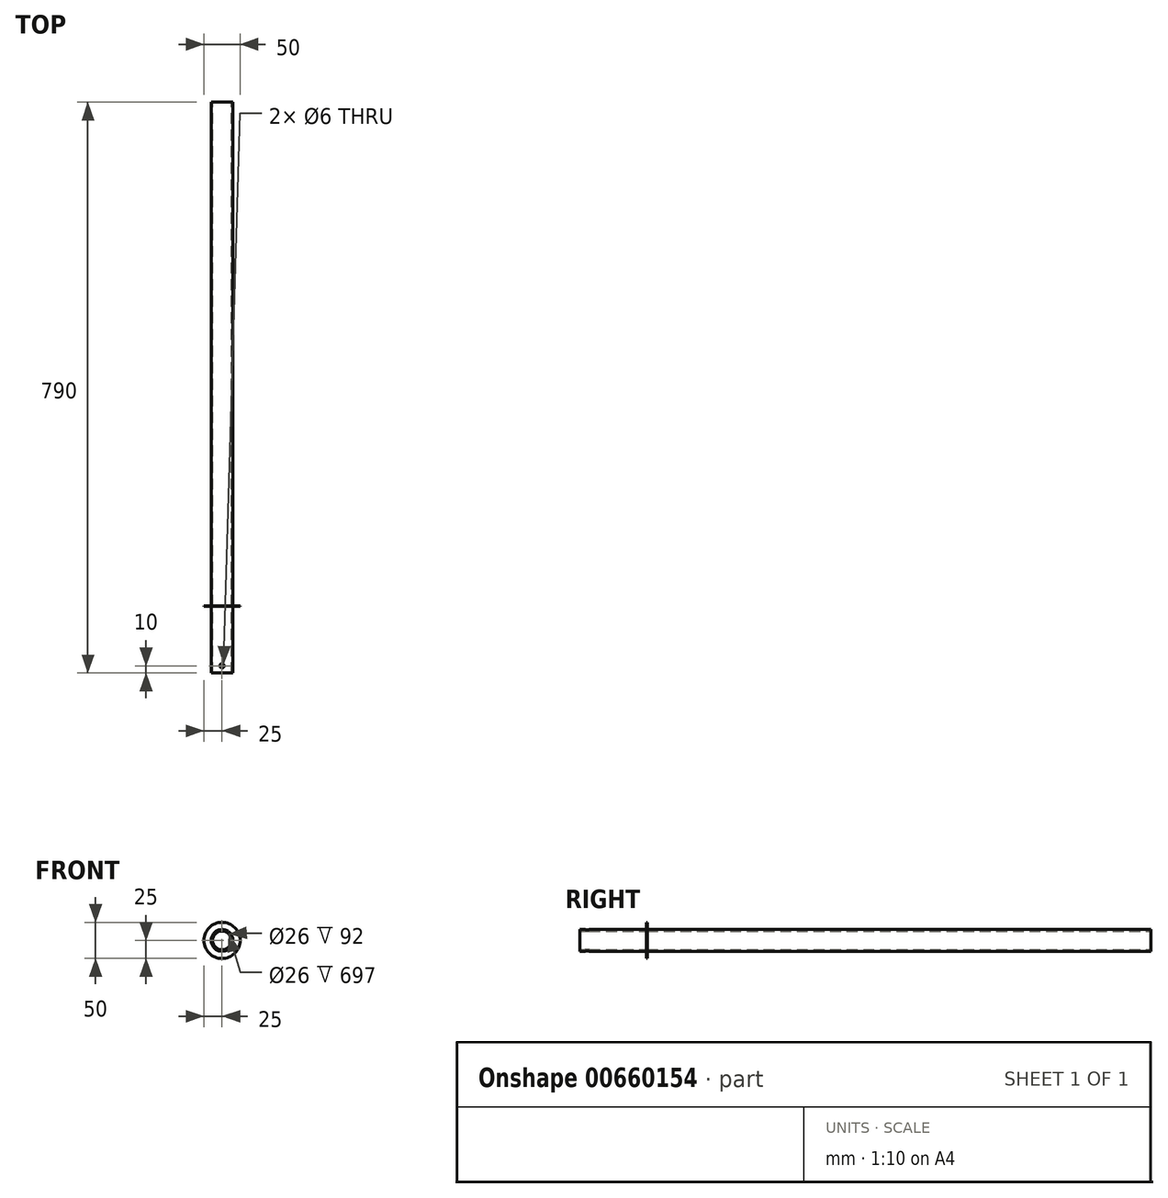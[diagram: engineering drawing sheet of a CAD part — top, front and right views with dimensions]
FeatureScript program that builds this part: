
annotation { "Feature Type Name" : "Feature", "Feature Type Description" : "" }
export const myFeature = defineFeature(function(context is Context, id is Id, definition is map)
    precondition{}
    {
        {
            var Q0;
            Q0=qCreatedBy(makeId("Front.planeOp"),FACE);
            var sketch = newSketch(context, id + "F0", { "sketchPlane" : qUnion([Q0])});
            skCircle(sketch, "E0", {"center": v(0, 0) * mm, "radius": 15 * mm});
            skCircle(sketch, "E1.0", {"center": v(0, 0) * mm, "radius": 13 * mm});
            skSolve(sketch);
        }
        {
            var Q0;
            Q0=makeQuery(id+"F0.imprint","IMPRINT",FACE,{"disambiguationData":[TD([[makeQuery(id+"F0.imprint","IMPRINT",EDGE,{"derivedFrom":sQuery(id+"F0.wireOp",EDGE,"E0")}),1.0]])]});
            extrude(context, id + "F1", {"entities" : qUnion([Q0]), "depth" : 790 * mm, "symmetric" : true});
        }
        {
            var Q0;
            Q0=makeQuery(id+"F1.opExtrude","CAP_FACE",FACE,{"disambiguationData":[OSD([sQuery(id+"F0.wireOp",EDGE,"E0"),sQuery(id+"F0.wireOp",EDGE,"E1.0")])],"isStart":false});
            cPlane(context, id + "F2", {"entities" : qUnion([Q0]), "cplaneType" : CPlaneType.OFFSET, "offset" : 92 * mm, "oppositeDirection" : true, "width" : 150 * mm, "height" : 150 * mm});
        }
        {
            var Q0;
            Q0=qCreatedBy(id+"F2.planeOp",FACE);
            var sketch = newSketch(context, id + "F3", { "sketchPlane" : qUnion([Q0])});
            skCircle(sketch, "E2", {"center": v(0, 0) * mm, "radius": 25 * mm});
            skSolve(sketch);
        }
        {
            var Q0;
            Q0=makeQuery(id+"F3.imprint","IMPRINT",FACE,{"disambiguationData":[TD([[makeQuery(id+"F3.imprint","IMPRINT",EDGE,{"derivedFrom":sQuery(id+"F3.wireOp",EDGE,"E2")}),1.0]])]});
            extrude(context, id + "F4", {"entities" : qUnion([Q0]), "operationType" : NewBodyOperationType.ADD, "oppositeDirection" : true, "depth" : 1 * mm});
        }
        {
            var Q0;
            Q0=qCreatedBy(makeId("Top.planeOp"),FACE);
            var sketch = newSketch(context, id + "F5", { "sketchPlane" : qUnion([Q0])});
            skPoint(sketch, "E3", {"position": v(0, -385) * mm});
            skLineSegment(sketch, "E4", {"start": v(15, -300) * mm, "end": v(15, -395) * mm});
            skLineSegment(sketch, "E5", {"start": v(-15, -395) * mm, "end": v(-15, -300) * mm});
            skLineSegment(sketch, "E6.0", {"start": v(15, -395) * mm, "end": v(-15, -395) * mm});
            skSolve(sketch);
        }
        {
            var Q0;
            Q0=sQuery(id+"F5.wireOp",VERTEX,"E3");
            var Q1;
            Q1=makeQuery(id+"F1.opExtrude","SWEPT_BODY",BODY,{"disambiguationData":[OSD([sQuery(id+"F0.wireOp",EDGE,"E0"),sQuery(id+"F0.wireOp",EDGE,"E1.0")])]});
            hole(context, id + "F6", {"style" : HoleStyle.SIMPLE, "endStyle" : HoleEndStyle.THROUGH, "holeDiameter" : 6 * mm, "tappedDepth" : 12 * mm, "tapClearance" : 1, "locations" : qUnion([Q0]), "scope" : qUnion([Q1])});
        }
        {
            var Q0;
            Q0=sQuery(id+"F5.wireOp",VERTEX,"E3");
            var Q1;
            Q1=makeQuery(id+"F1.opExtrude","SWEPT_BODY",BODY,{"disambiguationData":[OSD([sQuery(id+"F0.wireOp",EDGE,"E0"),sQuery(id+"F0.wireOp",EDGE,"E1.0")])]});
            hole(context, id + "F7", {"style" : HoleStyle.SIMPLE, "endStyle" : HoleEndStyle.THROUGH, "oppositeDirection" : true, "holeDiameter" : 6 * mm, "tappedDepth" : 12 * mm, "tapClearance" : 1, "locations" : qUnion([Q0]), "scope" : qUnion([Q1])});
        }
    });
